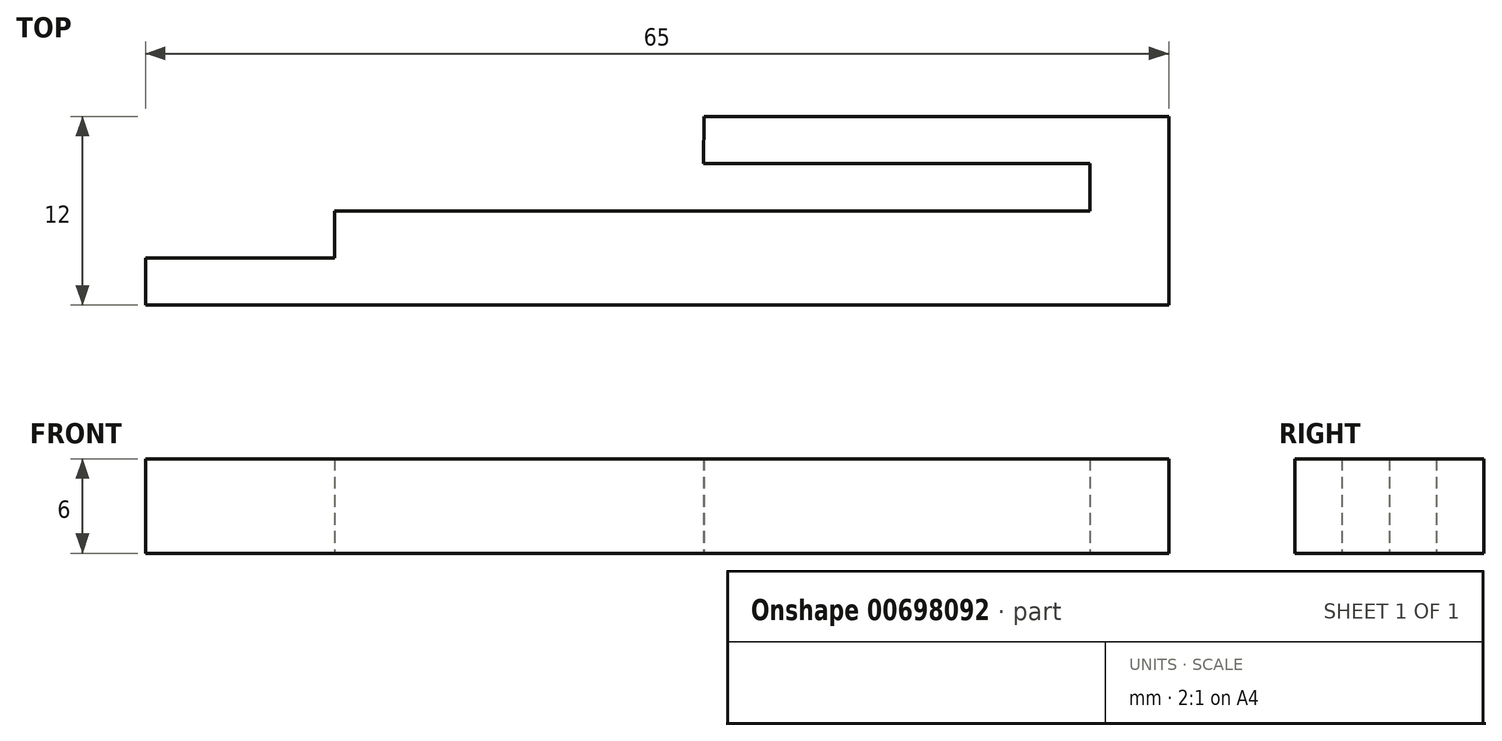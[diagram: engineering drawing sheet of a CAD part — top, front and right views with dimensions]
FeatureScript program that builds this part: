
annotation { "Feature Type Name" : "Feature", "Feature Type Description" : "" }
export const myFeature = defineFeature(function(context is Context, id is Id, definition is map)
    precondition{}
    {
        {
            var Q0;
            Q0=qCreatedBy(makeId("Top.planeOp"),FACE);
            var sketch = newSketch(context, id + "F0", { "sketchPlane" : qUnion([Q0])});
            skLineSegment(sketch, "E0", {"start": v(-19.61, 9) * mm, "end": v(4.93, 9) * mm});
            skLineSegment(sketch, "E1", {"start": v(4.93, 9) * mm, "end": v(4.93, 6) * mm});
            skLineSegment(sketch, "E2", {"start": v(4.93, 6) * mm, "end": v(-43.07, 6) * mm});
            skLineSegment(sketch, "E3", {"start": v(-43.07, 6) * mm, "end": v(-43.07, 3) * mm});
            skLineSegment(sketch, "E4", {"start": v(-43.07, 3) * mm, "end": v(-55.07, 3) * mm});
            skLineSegment(sketch, "E5", {"start": v(-55.07, 3) * mm, "end": v(-55.07, 0) * mm});
            skLineSegment(sketch, "E6", {"start": v(-55.07, 0) * mm, "end": v(9.93, 0) * mm});
            skLineSegment(sketch, "E7", {"start": v(9.93, 0) * mm, "end": v(9.93, 12) * mm});
            skLineSegment(sketch, "E8", {"start": v(9.93, 12) * mm, "end": v(-19.6, 12) * mm});
            skLineSegment(sketch, "E9", {"start": v(-19.6, 12) * mm, "end": v(-19.61, 9) * mm});
            skSolve(sketch);
        }
        {
            var Q0;
            Q0 = qSketchRegion(id + "F0", true);
            extrude(context, id + "F1", {"entities" : qUnion([Q0]), "depth" : 6 * mm, "offsetDistance" : 25 * mm});
        }
    });
